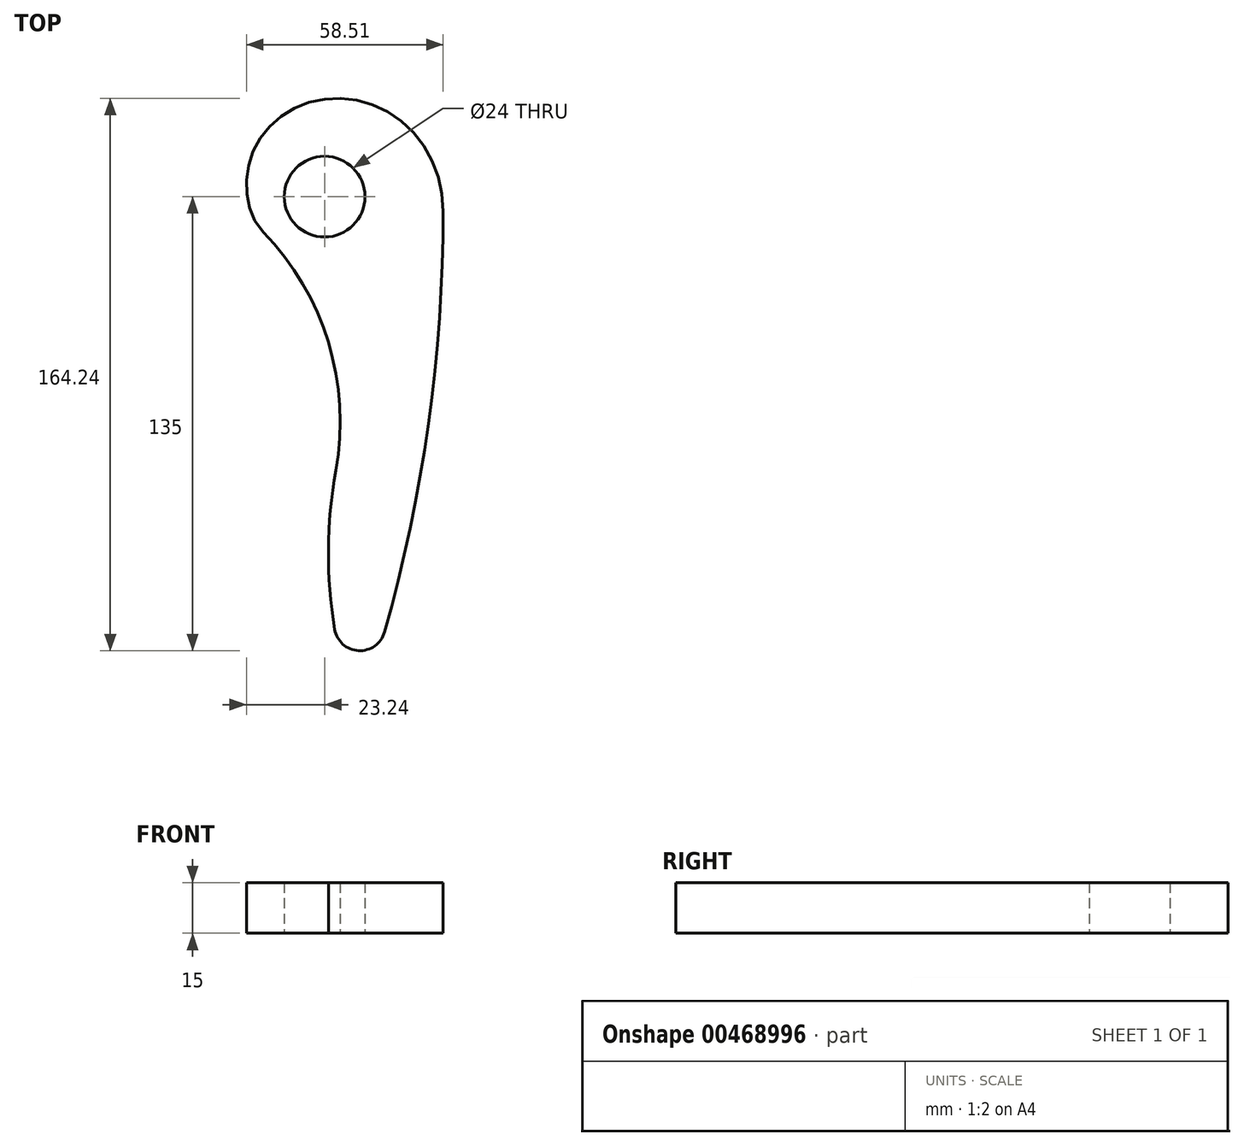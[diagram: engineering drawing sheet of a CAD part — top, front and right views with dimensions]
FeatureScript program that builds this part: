
annotation { "Feature Type Name" : "Feature", "Feature Type Description" : "" }
export const myFeature = defineFeature(function(context is Context, id is Id, definition is map)
    precondition{}
    {
        {
            var Q0;
            Q0=qCreatedBy(makeId("Top.planeOp"),FACE);
            var sketch = newSketch(context, id + "F0", { "sketchPlane" : qUnion([Q0])});
            skCircle(sketch, "E0", {"center": v(0, 0) * mm, "radius": 9.5 * mm});
            skSolve(sketch);
        }
        {
            var Q0;
            Q0=makeQuery(id+"F0.imprint","IMPRINT",FACE,{"disambiguationData":[TD([[makeQuery(id+"F0.imprint","IMPRINT",EDGE,{"derivedFrom":sQuery(id+"F0.wireOp",EDGE,"E0")}),1.0]])]});
            var sketch = newSketch(context, id + "F1", { "sketchPlane" : qUnion([Q0])});
            skCircle(sketch, "E1", {"center": v(0, 0) * mm, "radius": 35 * mm, "construction": true});
            skLineSegment(sketch, "E2", {"start": v(0, 0) * mm, "end": v(-35, 0) * mm, "construction": true});
            skLineSegment(sketch, "E3.1.0", {"start": v(0, 0) * mm, "end": v(-30.31, -17.5) * mm, "construction": true});
            skLineSegment(sketch, "E3.2.0", {"start": v(0, 0) * mm, "end": v(-17.5, -30.31) * mm, "construction": true});
            skLineSegment(sketch, "E3.3.0", {"start": v(0, 0) * mm, "end": v(0, -35) * mm, "construction": true});
            skLineSegment(sketch, "E3.4.0", {"start": v(0, 0) * mm, "end": v(17.5, -30.31) * mm, "construction": true});
            skLineSegment(sketch, "E3.5.0", {"start": v(0, 0) * mm, "end": v(30.31, -17.5) * mm, "construction": true});
            skLineSegment(sketch, "E3.6.0", {"start": v(0, 0) * mm, "end": v(35, 0) * mm, "construction": true});
            skLineSegment(sketch, "E3.7.0", {"start": v(0, 0) * mm, "end": v(30.31, 17.5) * mm, "construction": true});
            skLineSegment(sketch, "E3.8.0", {"start": v(0, 0) * mm, "end": v(17.5, 30.31) * mm, "construction": true});
            skLineSegment(sketch, "E3.9.0", {"start": v(0, 0) * mm, "end": v(0, 35) * mm, "construction": true});
            skLineSegment(sketch, "E3.10.0", {"start": v(0, 0) * mm, "end": v(-17.5, 30.31) * mm, "construction": true});
            skLineSegment(sketch, "E3.11.0", {"start": v(0, 0) * mm, "end": v(-30.31, 17.5) * mm, "construction": true});
            skPoint(sketch, "E4", {"position": v(28.58, 16.5) * mm});
            skPoint(sketch, "E5", {"position": v(15.5, 26.85) * mm});
            skPoint(sketch, "E6", {"position": v(0, 29) * mm});
            skPoint(sketch, "E7", {"position": v(-13.5, 23.38) * mm});
            skPoint(sketch, "E8", {"position": v(-21.65, 12.5) * mm});
            skPoint(sketch, "E9", {"position": v(-23, 0) * mm});
            skPoint(sketch, "E10", {"position": v(-18.19, -10.5) * mm});
            skPoint(sketch, "E11", {"position": v(32.04, -18.5) * mm});
            skPoint(sketch, "E12", {"position": v(19.5, -33.77) * mm});
            skPoint(sketch, "E13", {"position": v(30.31, -17.5) * mm});
            skLineSegment(sketch, "E14", {"start": v(30.31, -17.5) * mm, "end": v(32.65, -18.85) * mm, "construction": true});
            skLineSegment(sketch, "E15", {"start": v(17.5, -30.31) * mm, "end": v(20.98, -36.33) * mm, "construction": true});
            skFitSpline(sketch, "E16", {"points": [v(19.5, -33.77) * mm, v(32.04, -18.5) * mm, v(35, 0) * mm, v(28.58, 16.5) * mm, v(15.5, 26.85) * mm, v(0, 29) * mm, v(-13.5, 23.38) * mm, v(-21.65, 12.5) * mm, v(-23, 0) * mm, v(-18.19, -10.5) * mm, v(-7.77, -17.61) * mm], "startDerivative": vector(113.63, 73.96) * mm, "endDerivative": vector(86.95, -47.22) * mm});
            skLineSegment(sketch, "E17", {"start": v(35.27, 29.24) * mm, "end": v(35.27, -4.3) * mm, "construction": true});
            skLineSegment(sketch, "E18", {"start": v(-23.24, 29.24) * mm, "end": v(-23.24, -135) * mm, "construction": true});
            skLineSegment(sketch, "E19", {"start": v(-23.24, 29.24) * mm, "end": v(35.27, 29.24) * mm, "construction": true});
            skPoint(sketch, "E20", {"position": v(3.74, 29.24) * mm});
            skPoint(sketch, "E21", {"position": v(35.27, -4.3) * mm});
            skPoint(sketch, "E22", {"position": v(-23.24, 3.6) * mm});
            skLineSegment(sketch, "E23", {"start": v(-23.24, -135) * mm, "end": v(35.27, -135) * mm, "construction": true});
            skLineSegment(sketch, "E24", {"start": v(35.27, -4.3) * mm, "end": v(35.27, -135) * mm, "construction": true});
            skArc(sketch, "E25", {"start": v(35.27, -4.3) * mm, "mid": v(30.48, -70.34) * mm, "end": v(16.22, -135) * mm});
            skArc(sketch, "E26.0", {"start": v(10.27, -4.3) * mm, "mid": v(5.19, -70.43) * mm, "end": v(-9.93, -135) * mm, "construction": true});
            skArc(sketch, "E27", {"start": v(3.34, -81.44) * mm, "mid": v(1.14, -43.37) * mm, "end": v(-18.19, -10.5) * mm});
            skArc(sketch, "E28", {"start": v(3.34, -81.44) * mm, "mid": v(1.15, -108.26) * mm, "end": v(4.22, -135) * mm});
            skArc(sketch, "E29", {"start": v(3, -128.64) * mm, "mid": v(10.08, -134.99) * mm, "end": v(17.83, -129.47) * mm});
            skCircle(sketch, "E30.0", {"center": v(0, 0) * mm, "radius": 9.5 * mm});
            skCircle(sketch, "E31", {"center": v(0, 0) * mm, "radius": 12 * mm});
            skSolve(sketch);
        }
        {
            var Q0;
            {var subQ1=sQuery(id+"F1.wireOp",EDGE,"E27");Q0=makeQuery(id+"F1.imprint","IMPRINT",FACE,{"disambiguationData":[TD([[makeQuery(id+"F1.imprint","IMPRINT",EDGE,{"derivedFrom":subQ1}),-1.0]])]});}
            extrude(context, id + "F2", {"entities" : qUnion([Q0]), "depth" : 15 * mm});
        }
    });
